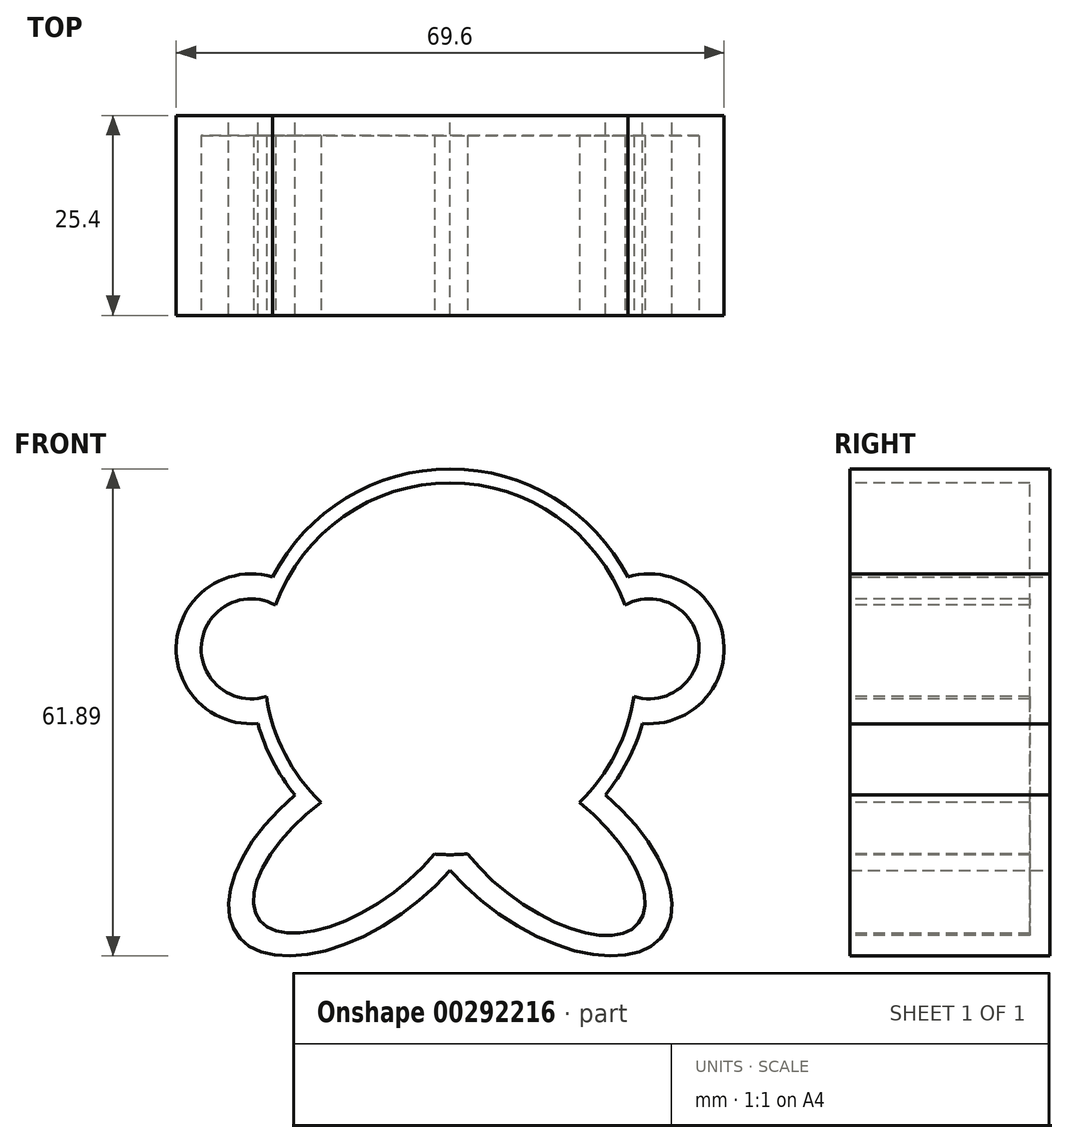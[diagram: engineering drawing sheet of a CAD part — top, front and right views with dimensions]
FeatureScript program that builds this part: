
annotation { "Feature Type Name" : "Feature", "Feature Type Description" : "" }
export const myFeature = defineFeature(function(context is Context, id is Id, definition is map)
    precondition{}
    {
        {
            var Q0;
            Q0=qCreatedBy(makeId("Front.planeOp"),FACE);
            var sketch = newSketch(context, id + "F0", { "sketchPlane" : qUnion([Q0])});
            skCircle(sketch, "E0", {"center": v(0, 0) * mm, "radius": 25.4 * mm});
            skEllipticalArc(sketch, "E1", {});
            skEllipticalArc(sketch, "E2.MirrorC", {});
            skArc(sketch, "E3.MirrorC", {"start": v(22.56, 11.67) * mm, "mid": v(34.75, 3.5) * mm, "end": v(24.43, -6.95) * mm});
            skArc(sketch, "E4.MirrorC", {"start": v(-24.43, -6.95) * mm, "mid": v(-34.75, 3.5) * mm, "end": v(-22.56, 11.67) * mm});
            const initialGuessF0  = {"E1": [-0.01165179370470863, -0.022569796265427662, -0.8071780050085969, -0.5903081129633417, 0.01905, 0.01016, 4.85139992565874, 1.9961590293744618], "E2.MirrorC": [0.01165179370470863, -0.022569796265427662, 0.8071780050085969, -0.5903081129633417, 0.01905, 0.01016, 4.287026277805124, 1.4317853815208468], "E1": [-0.01165179370470863, -0.022569796265427662, -0.8071780050085969, -0.5903081129633417, 0.01905, 0.01016, 4.85139992565874, 1.9961590293744618], "E2.MirrorC": [0.01165179370470863, -0.022569796265427662, 0.8071780050085969, -0.5903081129633417, 0.01905, 0.01016, 4.287026277805124, 1.4317853815208468]};
            skSetInitialGuess(sketch, initialGuessF0);
            skSolve(sketch);
        }
        {
            var Q0;
            Q0 = qSketchRegion(id + "F0", true);
            extrude(context, id + "F1", {"entities" : qUnion([Q0]), "depth" : 25.4 * mm});
        }
        {
            var Q0;
            Q0=makeQuery(id+"F1.opExtrude","CAP_FACE",FACE,{"disambiguationData":[OSD([sQuery(id+"F0.wireOp",EDGE,"E0"),sQuery(id+"F0.wireOp",EDGE,"E3.MirrorC"),sQuery(id+"F0.wireOp",EDGE,"E1"),sQuery(id+"F0.wireOp",EDGE,"E4.MirrorC"),sQuery(id+"F0.wireOp",EDGE,"E2.MirrorC")])],"isStart":false});
            var sketch = newSketch(context, id + "F2", { "sketchPlane" : qUnion([Q0])});
            skCircle(sketch, "E5", {"center": v(0, 0) * mm, "radius": 23.61 * mm});
            skArc(sketch, "E6", {"start": v(23.35, -3.51) * mm, "mid": v(31.6, 3.17) * mm, "end": v(22.19, 8.09) * mm});
            skPoint(sketch, "E7.center.orphan", {"position": v(-44.67, -6.95) * mm});
            skPoint(sketch, "E8.center.orphan", {"position": v(-17.7, 2.54) * mm});
            skPoint(sketch, "E9.center.orphan", {"position": v(-25.27, 2.54) * mm});
            skArc(sketch, "E10", {"start": v(-22.19, 8.09) * mm, "mid": v(-31.6, 3.18) * mm, "end": v(-23.35, -3.51) * mm});
            skEllipticalArc(sketch, "E11", {});
            skEllipticalArc(sketch, "E12", {});
            const initialGuessF2  = {"E11": [-0.01165179370470863, -0.022569796265427662, -0.8039627060199951, -0.5946797182761551, 0.0156718, 0.0073533, 4.744697604175021, 2.0488017541508388], "E12": [0.01165179370470863, -0.022569796265427662, 0.7843777439345496, -0.6202834471595595, 0.0156718, 0.0073533, 4.260472581198911, 1.5537072210787644]};
            skSetInitialGuess(sketch, initialGuessF2);
            skSolve(sketch);
        }
        {
            var Q0;
            Q0 = qSketchRegion(id + "F2", true);
            extrude(context, id + "F3", {"entities" : qUnion([Q0]), "operationType" : NewBodyOperationType.REMOVE, "oppositeDirection" : true, "depth" : 22.86 * mm});
        }
    });
